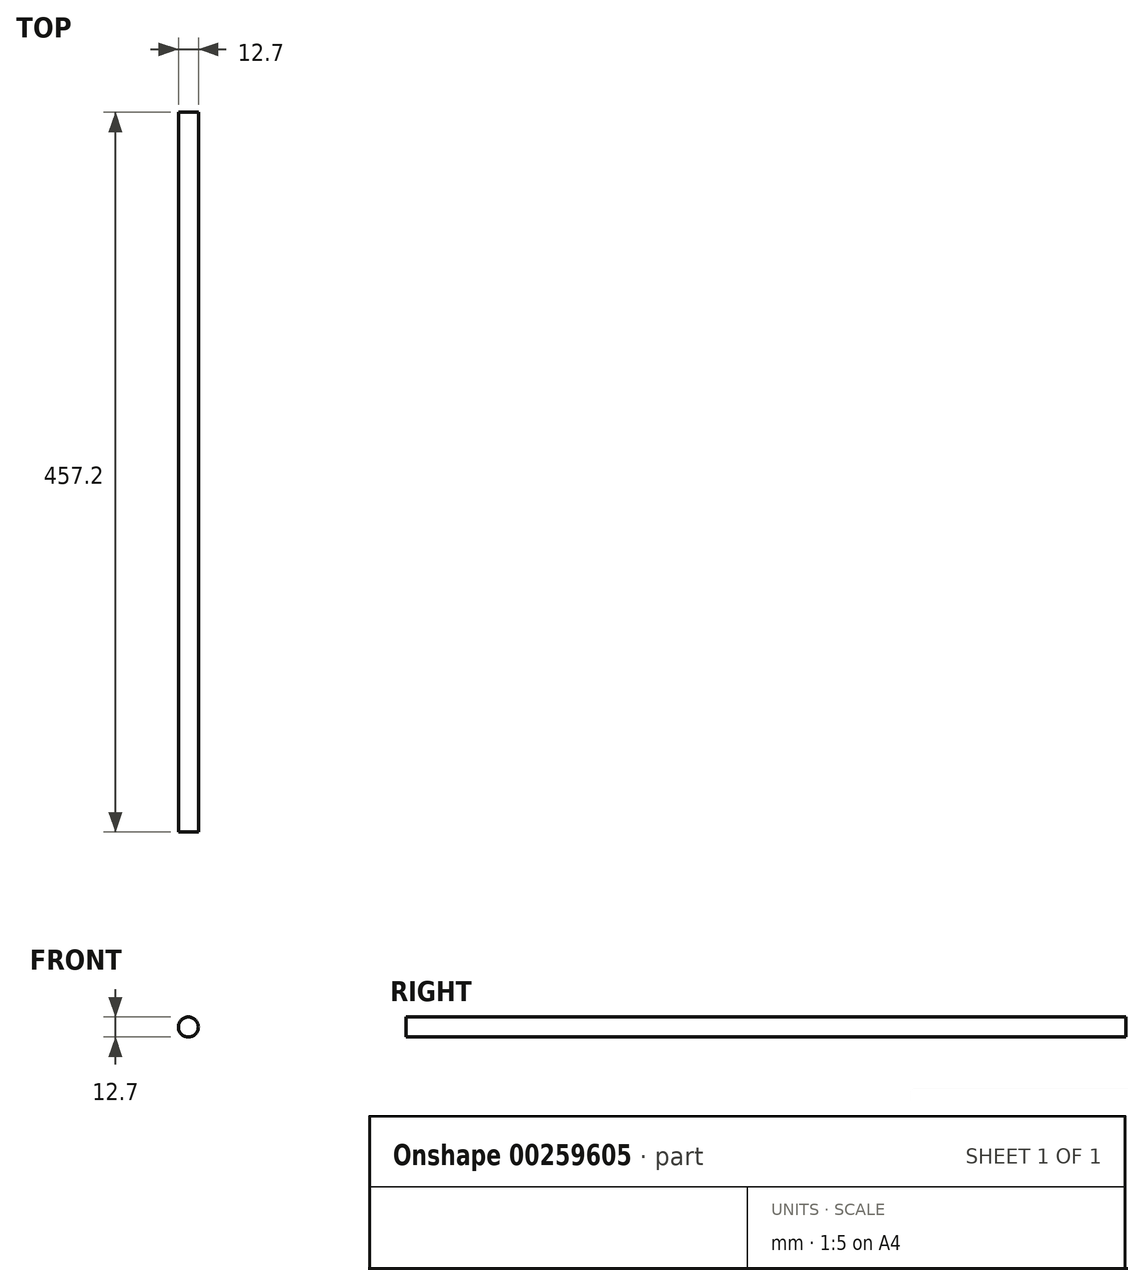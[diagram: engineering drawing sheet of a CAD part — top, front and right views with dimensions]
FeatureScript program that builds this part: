
annotation { "Feature Type Name" : "Feature", "Feature Type Description" : "" }
export const myFeature = defineFeature(function(context is Context, id is Id, definition is map)
    precondition{}
    {
        {
            var Q0;
            Q0=qCreatedBy(makeId("Front.planeOp"),FACE);
            var sketch = newSketch(context, id + "F0", { "sketchPlane" : qUnion([Q0])});
            skCircle(sketch, "E0", {"center": v(0, 0) * mm, "radius": 6.35 * mm});
            skSolve(sketch);
        }
        {
            var Q0;
            Q0=makeQuery(id+"F0.imprint","IMPRINT",FACE,{"disambiguationData":[TD([[makeQuery(id+"F0.imprint","IMPRINT",EDGE,{"derivedFrom":sQuery(id+"F0.wireOp",EDGE,"E0")}),1.0]])]});
            extrude(context, id + "F1", {"entities" : qUnion([Q0]), "depth" : 457.2 * mm, "symmetric" : true});
        }
    });
